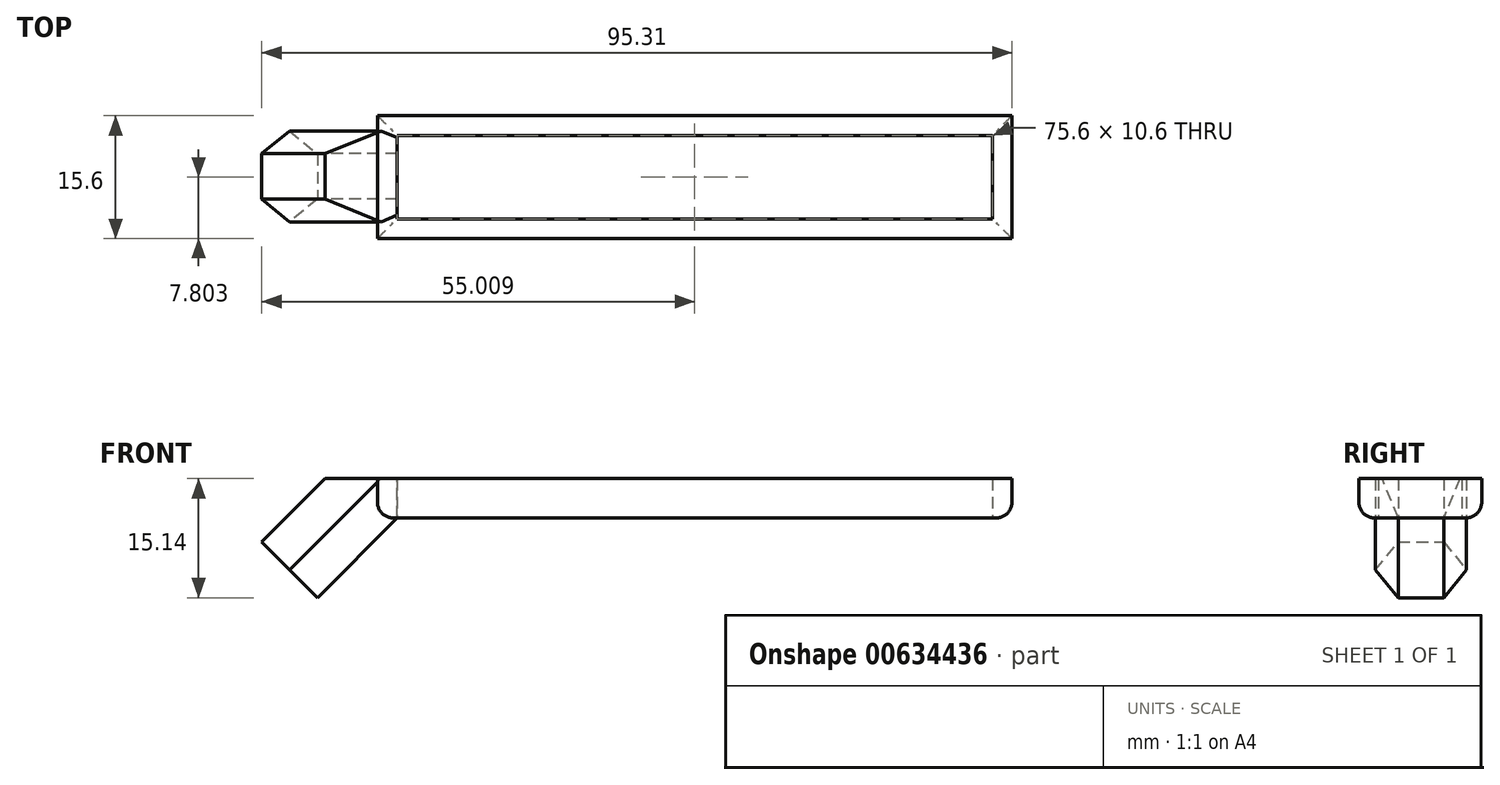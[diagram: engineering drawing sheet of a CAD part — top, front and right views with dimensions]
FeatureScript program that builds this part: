
annotation { "Feature Type Name" : "Feature", "Feature Type Description" : "" }
export const myFeature = defineFeature(function(context is Context, id is Id, definition is map)
    precondition{}
    {
        {
            var Q0;
            Q0=qCreatedBy(makeId("Top.planeOp"),FACE);
            var sketch = newSketch(context, id + "F0", { "sketchPlane" : qUnion([Q0])});
            skLineSegment(sketch, "E0", {"start": v(-15.54, -10.59) * mm, "end": v(60.06, -10.59) * mm});
            skLineSegment(sketch, "E1", {"start": v(-15.54, 0.01) * mm, "end": v(60.06, 0.01) * mm});
            skLineSegment(sketch, "E2", {"start": v(60.06, 0.01) * mm, "end": v(60.06, -10.59) * mm});
            skLineSegment(sketch, "E3", {"start": v(-15.54, 0.01) * mm, "end": v(-15.54, -10.59) * mm});
            skLineSegment(sketch, "E4.0", {"start": v(-18.04, 2.51) * mm, "end": v(62.56, 2.51) * mm});
            skLineSegment(sketch, "E4.1", {"start": v(-18.04, 2.51) * mm, "end": v(-18.04, -13.09) * mm});
            skLineSegment(sketch, "E4.2", {"start": v(-18.04, -13.09) * mm, "end": v(62.56, -13.09) * mm});
            skLineSegment(sketch, "E4.3", {"start": v(62.56, 2.51) * mm, "end": v(62.56, -13.09) * mm});
            skSolve(sketch);
        }
        {
            var Q0;
            Q0=makeQuery(id+"F0.imprint","IMPRINT",FACE,{"disambiguationData":[TD([[makeQuery(id+"F0.imprint","IMPRINT",EDGE,{"derivedFrom":sQuery(id+"F0.wireOp",EDGE,"E0")}),-1.0]])]});
            extrude(context, id + "F1", {"entities" : qUnion([Q0]), "depth" : 5 * mm, "offsetDistance" : 25 * mm});
        }
        {
            var Q0;
            Q0=makeQuery(id+"F1.opExtrude","CAP_EDGE",EDGE,{"disambiguationData":[OSD([sQuery(id+"F0.wireOp",EDGE,"E4.2")])],"isStart":true});
            var Q1;
            Q1=makeQuery(id+"F1.opExtrude","CAP_EDGE",EDGE,{"disambiguationData":[OSD([sQuery(id+"F0.wireOp",EDGE,"E4.1")])],"isStart":true});
            var Q2;
            Q2=makeQuery(id+"F1.opExtrude","CAP_EDGE",EDGE,{"disambiguationData":[OSD([sQuery(id+"F0.wireOp",EDGE,"E4.0")])],"isStart":true});
            var Q3;
            Q3=makeQuery(id+"F1.opExtrude","CAP_EDGE",EDGE,{"disambiguationData":[OSD([sQuery(id+"F0.wireOp",EDGE,"E4.3")])],"isStart":true});
            fillet(context, id + "F2", {"entities" : qUnion([Q0, Q1, Q2, Q3]), "radius" : 2 * mm, "tangentPropagation" : true, "allowEdgeOverflow" : false});
        }
        {
            var Q0;
            Q0=qCreatedBy(makeId("Top.planeOp"),FACE);
            var sketch = newSketch(context, id + "F3", { "sketchPlane" : qUnion([Q0])});
            skCircle(sketch, "E5.cCircle", {"center": v(-13.33, 0) * mm, "radius": 5 * mm, "construction": true});
            skLineSegment(sketch, "E5.0", {"start": v(-8.33, 2.89) * mm, "end": v(-8.33, -2.89) * mm});
            skLineSegment(sketch, "E5.1", {"start": v(-8.33, -2.89) * mm, "end": v(-13.33, -5.77) * mm});
            skLineSegment(sketch, "E5.2", {"start": v(-13.33, -5.77) * mm, "end": v(-18.33, -2.89) * mm});
            skLineSegment(sketch, "E5.3", {"start": v(-18.33, -2.89) * mm, "end": v(-18.33, 2.89) * mm});
            skLineSegment(sketch, "E5.4", {"start": v(-18.33, 2.89) * mm, "end": v(-13.33, 5.77) * mm});
            skLineSegment(sketch, "E5.5", {"start": v(-13.33, 5.77) * mm, "end": v(-8.33, 2.89) * mm});
            skPoint(sketch, "E5.0.midPoint", {"position": v(-8.33, 0) * mm});
            skSolve(sketch);
        }
        {
            var Q0;
            Q0=qSketchRegion(id+"F3",true);
            extrude(context, id + "F4", {"entities" : qUnion([Q0]), "depth" : 4 * mm, "offsetDistance" : 25 * mm, "hasSecondDirection" : true, "secondDirectionOppositeDirection" : true, "secondDirectionDepth" : 16 * mm});
        }
        {
            var Q0;
            Q0=makeQuery(id+"F4.opExtrude","SWEPT_BODY",BODY,{"disambiguationData":[OSD([sQuery(id+"F3.wireOp",EDGE,"E5.0"),sQuery(id+"F3.wireOp",EDGE,"E5.1"),sQuery(id+"F3.wireOp",EDGE,"E5.2"),sQuery(id+"F3.wireOp",EDGE,"E5.3"),sQuery(id+"F3.wireOp",EDGE,"E5.4"),sQuery(id+"F3.wireOp",EDGE,"E5.5")])]});
            var Q1;
            Q1=makeQuery(id+"F4.opExtrude","CAP_EDGE",EDGE,{"disambiguationData":[OSD([sQuery(id+"F3.wireOp",EDGE,"E5.0")])],"isStart":false});
            transform(context, id + "F5", {"entities" : qUnion([Q0]), "transformType" : TransformType.ROTATION, "transformAxis" : qUnion([Q1]), "angle" : 45 * degree, "oppositeDirection" : true, "makeCopy" : false});
        }
        {
            var Q0;
            Q0=makeQuery(id+"F4.opExtrude","SWEPT_BODY",BODY,{"disambiguationData":[OSD([sQuery(id+"F3.wireOp",EDGE,"E5.0"),sQuery(id+"F3.wireOp",EDGE,"E5.1"),sQuery(id+"F3.wireOp",EDGE,"E5.2"),sQuery(id+"F3.wireOp",EDGE,"E5.3"),sQuery(id+"F3.wireOp",EDGE,"E5.4"),sQuery(id+"F3.wireOp",EDGE,"E5.5")])]});
            transform(context, id + "F6", {"entities" : qUnion([Q0]), "transformType" : TransformType.TRANSLATION_3D, "dx" : -3.2 * mm, "dy" : -5.2 * mm, "dz" : 0 * mm, "makeCopy" : false});
        }
        {
            var Q0;
            Q0=makeQuery(id+"F0.imprint","IMPRINT",FACE,{"disambiguationData":[TD([[makeQuery(id+"F0.imprint","IMPRINT",EDGE,{"derivedFrom":sQuery(id+"F0.wireOp",EDGE,"E0")}),1.0]])]});
            extrude(context, id + "F7", {"entities" : qUnion([Q0]), "operationType" : NewBodyOperationType.REMOVE, "depth" : 10 * mm, "offsetDistance" : 25 * mm, "hasSecondDirection" : true, "secondDirectionOppositeDirection" : true, "secondDirectionDepth" : 4 * mm});
        }
        {
            var Q0;
            Q0=makeQuery(id+"F1.opExtrude","CAP_FACE",FACE,{"disambiguationData":[OSD([sQuery(id+"F0.wireOp",EDGE,"E0"),sQuery(id+"F0.wireOp",EDGE,"E1"),sQuery(id+"F0.wireOp",EDGE,"9E00eGrz-qDNB-Kyzp-EWPo-orw2euIRPHMy"),sQuery(id+"F0.wireOp",EDGE,"LnV3E7uw-aS90-vI8X-CqTw-6LZ2jJMuHk54"),sQuery(id+"F0.wireOp",EDGE,"Mjp27t7W-bzR2-34PF-61Od-aDvYfcsOQjCj"),sQuery(id+"F0.wireOp",EDGE,"ewygOpiT-qmaV-T5hd-RivI-BRFqJAklPBYM"),sQuery(id+"F0.wireOp",EDGE,"b57fe8cc-adfa-4112-86e2-a793ce3a83f7.filletArc"),sQuery(id+"F0.wireOp",EDGE,"ba295eb0-e875-44ae-b57c-83a52182f12e.filletArc"),sQuery(id+"F0.wireOp",EDGE,"50cba6dd-6752-4126-822d-34af97ffccdd.0"),sQuery(id+"F0.wireOp",EDGE,"50cba6dd-6752-4126-822d-34af97ffccdd.1"),sQuery(id+"F0.wireOp",EDGE,"50cba6dd-6752-4126-822d-34af97ffccdd.2"),sQuery(id+"F0.wireOp",EDGE,"50cba6dd-6752-4126-822d-34af97ffccdd.3"),sQuery(id+"F0.wireOp",EDGE,"50cba6dd-6752-4126-822d-34af97ffccdd.4"),sQuery(id+"F0.wireOp",EDGE,"50cba6dd-6752-4126-822d-34af97ffccdd.5"),sQuery(id+"F0.wireOp",EDGE,"50cba6dd-6752-4126-822d-34af97ffccdd.6"),sQuery(id+"F0.wireOp",EDGE,"50cba6dd-6752-4126-822d-34af97ffccdd.7")])],"isStart":false});
            var sketch = newSketch(context, id + "F8", { "sketchPlane" : qUnion([Q0])});
            skLineSegment(sketch, "E6.bottom", {"start": v(-34.7, 7.79) * mm, "end": v(-8.78, 7.79) * mm});
            skLineSegment(sketch, "E6.top", {"start": v(-34.7, -14.68) * mm, "end": v(-8.78, -14.68) * mm});
            skLineSegment(sketch, "E6.left", {"start": v(-34.7, 7.79) * mm, "end": v(-34.7, -14.68) * mm});
            skLineSegment(sketch, "E6.right", {"start": v(-8.78, 7.79) * mm, "end": v(-8.78, -14.68) * mm});
            skSolve(sketch);
        }
        {
            var Q0;
            Q0=qSketchRegion(id+"F8",true);
            extrude(context, id + "F9", {"entities" : qUnion([Q0]), "operationType" : NewBodyOperationType.REMOVE, "depth" : 25 * mm, "offsetDistance" : 25 * mm});
        }
    });
